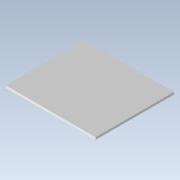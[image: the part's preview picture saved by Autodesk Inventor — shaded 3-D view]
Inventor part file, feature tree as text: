
AUTODESK INVENTOR PART (.ipt)
format: ipt  version: 2021 (Build 250183000, 183)  size: 89,088 bytes
history: native  units: mm
features: extrude x2, sketch x2, other x1
ambient origin geometry x8: Origin, YZ Plane, XZ Plane, XY Plane, X Axis, Y Axis, Z Axis, Center Point
bodies: Body1 (feature_tree)
feature tree (5):
  other  "Sólido1"
  extrude  "Extrusión1"  Depth=40.0mm
  extrude  "Extrusión2"  Depth=1.0mm
  sketch  "Boceto1"  dims[d1=60.0mm d3=40.0mm]
  sketch  "Boceto2"  dims[d4=1.0mm d5=0.0mm d7=44.0mm d8=9.0mm d9=0.0mm d10=0.0mm]
